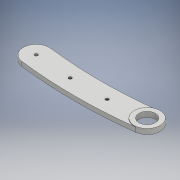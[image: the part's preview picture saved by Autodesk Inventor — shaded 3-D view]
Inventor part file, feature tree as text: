
AUTODESK INVENTOR PART (.ipt)
format: ipt  version: 2017 (Build 210142000, 142)  size: 278,016 bytes
history: native  units: mm
features: extrude x3, sketch x3, chamfer x1
ambient origin geometry x8: Origin, YZ Plane, XZ Plane, XY Plane, X Axis, Y Axis, Z Axis, Center Point
bodies: Solid1 (feature_tree)
feature tree (7):
  extrude  "Extrusion1"  Depth=603.023091mm
  extrude  "Extrusion2"  Depth=1.0mm TaperAngle=0.0deg
  extrude  "Extrusion3"  Depth=7.9mm
  chamfer  "Chamfer1"  Distance=3.0mm
  sketch  "Sketch2"  dims[d13=6.0mm d14=0.0mm d15=1.0mm d16=0.0mm]
  sketch  "Sketch3"  dims[d19=7.9mm d20=7.9mm d21=3.0mm d22=0.0mm d23=1.8mm d24=2.0mm d25=45.0deg]
  sketch  "Sketch1"  dims[d0=148.4mm d1=34.6mm d2=603.023091mm d6=49.466667mm d7=24.733333mm d8=4.3mm d9=4.3mm d10=4.3mm d12=22.0mm]
